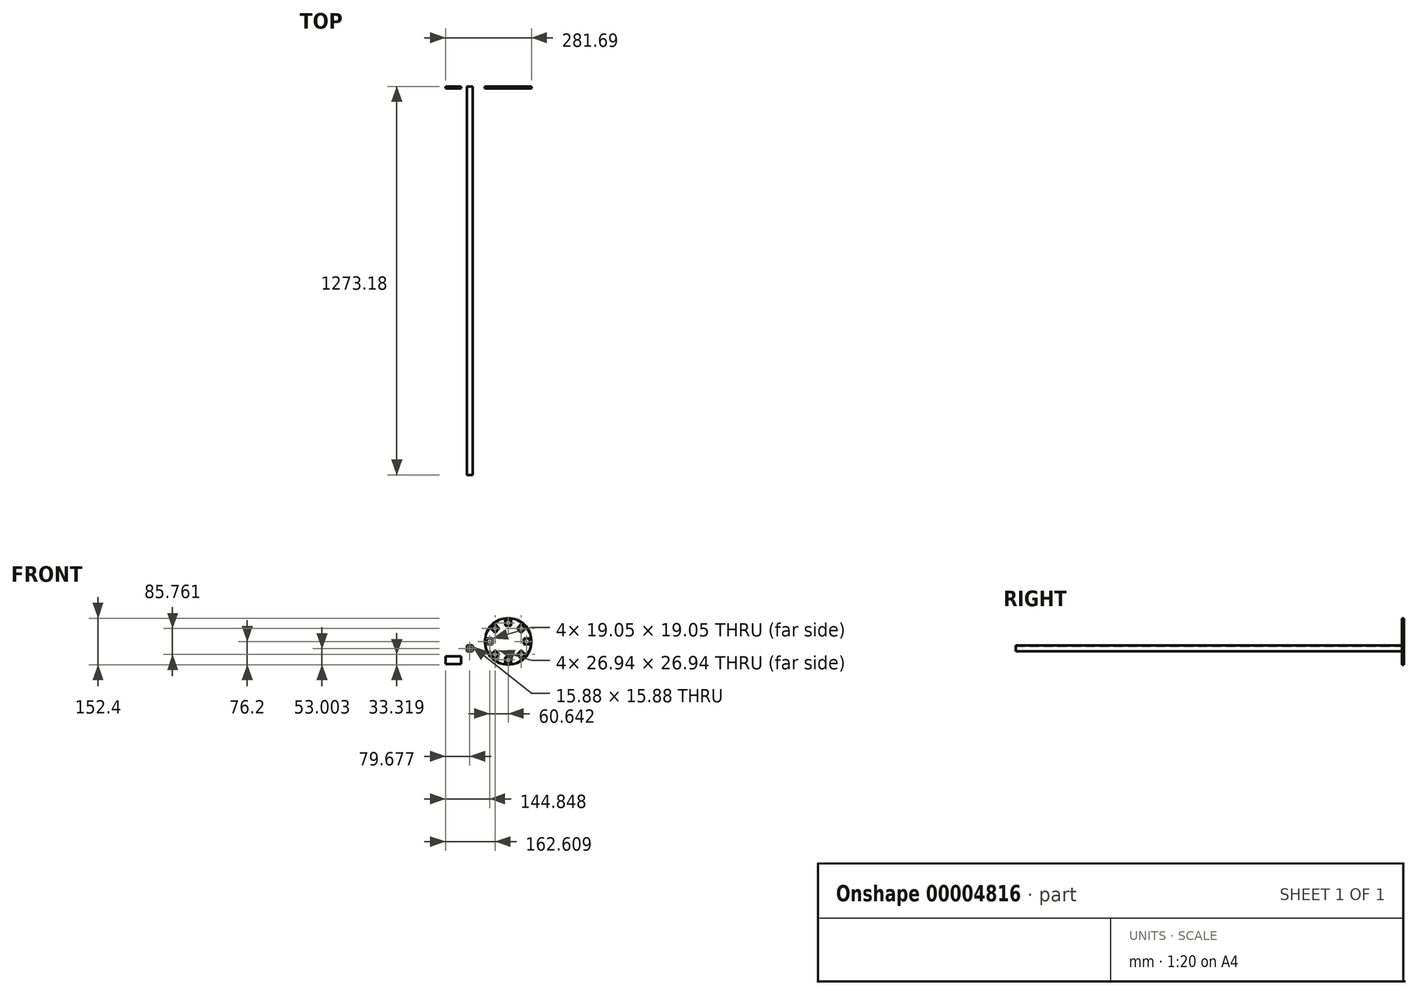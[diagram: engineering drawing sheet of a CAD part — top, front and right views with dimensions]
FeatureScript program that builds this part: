
annotation { "Feature Type Name" : "Feature", "Feature Type Description" : "" }
export const myFeature = defineFeature(function(context is Context, id is Id, definition is map)
    precondition{}
    {
        {
            var Q0;
            Q0=qCreatedBy(makeId("Front.planeOp"),FACE);
            var sketch = newSketch(context, id + "F0", { "sketchPlane" : qUnion([Q0])});
            skCircle(sketch, "E0", {"center": v(0, 0) * mm, "radius": 76.2 * mm});
            skLineSegment(sketch, "E1", {"start": v(0, 60.64) * mm, "end": v(0, 0) * mm, "construction": true});
            skLineSegment(sketch, "E2", {"start": v(123.6, 0) * mm, "end": v(-144.1, 0) * mm, "construction": true});
            skLineSegment(sketch, "E3.rect.bottom", {"start": v(9.53, 51.12) * mm, "end": v(-9.53, 51.12) * mm});
            skLineSegment(sketch, "E3.rect.top", {"start": v(9.53, 70.17) * mm, "end": v(-9.53, 70.17) * mm});
            skLineSegment(sketch, "E3.rect.left", {"start": v(9.52, 51.12) * mm, "end": v(9.53, 70.17) * mm});
            skLineSegment(sketch, "E3.rect.right", {"start": v(-9.53, 51.12) * mm, "end": v(-9.53, 70.17) * mm});
            skPoint(sketch, "E3.rect.middle", {"position": v(0, 60.64) * mm});
            skLineSegment(sketch, "E4.1.0", {"start": v(42.88, 56.35) * mm, "end": v(56.35, 42.88) * mm});
            skLineSegment(sketch, "E4.1.1", {"start": v(29.41, 42.88) * mm, "end": v(42.88, 29.41) * mm});
            skPoint(sketch, "E4.1.2", {"position": v(42.88, 42.88) * mm});
            skLineSegment(sketch, "E4.1.3", {"start": v(42.88, 56.35) * mm, "end": v(29.41, 42.88) * mm});
            skLineSegment(sketch, "E4.1.4", {"start": v(56.35, 42.88) * mm, "end": v(42.88, 29.41) * mm});
            skLineSegment(sketch, "E4.2.0", {"start": v(70.17, 9.53) * mm, "end": v(70.17, -9.53) * mm});
            skLineSegment(sketch, "E4.2.1", {"start": v(51.12, 9.53) * mm, "end": v(51.12, -9.52) * mm});
            skPoint(sketch, "E4.2.2", {"position": v(60.64, 0) * mm});
            skLineSegment(sketch, "E4.2.3", {"start": v(70.17, 9.52) * mm, "end": v(51.12, 9.52) * mm});
            skLineSegment(sketch, "E4.2.4", {"start": v(70.17, -9.53) * mm, "end": v(51.12, -9.53) * mm});
            skLineSegment(sketch, "E5.2.3.0", {"start": v(42.88, -56.35) * mm, "end": v(56.35, -42.88) * mm});
            skLineSegment(sketch, "E5.3.3.0", {"start": v(29.41, -42.88) * mm, "end": v(42.88, -29.41) * mm});
            skPoint(sketch, "E5.6.3.0", {"position": v(42.88, -42.88) * mm});
            skLineSegment(sketch, "E5.7.3.0", {"start": v(42.88, -29.41) * mm, "end": v(56.35, -42.88) * mm});
            skLineSegment(sketch, "E5.10.3.0", {"start": v(29.41, -42.88) * mm, "end": v(42.88, -56.35) * mm});
            skLineSegment(sketch, "E5.2.4.0", {"start": v(-9.52, -70.17) * mm, "end": v(9.53, -70.17) * mm});
            skLineSegment(sketch, "E5.3.4.0", {"start": v(-9.52, -51.12) * mm, "end": v(9.53, -51.12) * mm});
            skPoint(sketch, "E5.6.4.0", {"position": v(0, -60.64) * mm});
            skLineSegment(sketch, "E5.7.4.0", {"start": v(9.52, -51.12) * mm, "end": v(9.52, -70.17) * mm});
            skLineSegment(sketch, "E5.10.4.0", {"start": v(-9.52, -51.12) * mm, "end": v(-9.52, -70.17) * mm});
            skLineSegment(sketch, "E5.2.5.0", {"start": v(-42.88, -56.35) * mm, "end": v(-56.35, -42.88) * mm});
            skLineSegment(sketch, "E5.3.5.0", {"start": v(-29.41, -42.88) * mm, "end": v(-42.88, -29.41) * mm});
            skPoint(sketch, "E5.6.5.0", {"position": v(-42.88, -42.88) * mm});
            skLineSegment(sketch, "E5.7.5.0", {"start": v(-42.88, -56.35) * mm, "end": v(-29.41, -42.88) * mm});
            skLineSegment(sketch, "E5.10.5.0", {"start": v(-56.35, -42.88) * mm, "end": v(-42.88, -29.41) * mm});
            skLineSegment(sketch, "E5.2.6.0", {"start": v(-70.17, -9.53) * mm, "end": v(-70.17, 9.52) * mm});
            skLineSegment(sketch, "E5.3.6.0", {"start": v(-51.12, -9.53) * mm, "end": v(-51.12, 9.52) * mm});
            skPoint(sketch, "E5.6.6.0", {"position": v(-60.64, 0) * mm});
            skLineSegment(sketch, "E5.7.6.0", {"start": v(-70.17, -9.53) * mm, "end": v(-51.12, -9.53) * mm});
            skLineSegment(sketch, "E5.10.6.0", {"start": v(-70.17, 9.52) * mm, "end": v(-51.12, 9.52) * mm});
            skLineSegment(sketch, "E5.2.7.0", {"start": v(-42.88, 56.35) * mm, "end": v(-56.35, 42.88) * mm});
            skLineSegment(sketch, "E5.3.7.0", {"start": v(-29.41, 42.88) * mm, "end": v(-42.88, 29.41) * mm});
            skPoint(sketch, "E5.6.7.0", {"position": v(-42.88, 42.88) * mm});
            skLineSegment(sketch, "E5.7.7.0", {"start": v(-42.88, 29.41) * mm, "end": v(-56.35, 42.88) * mm});
            skLineSegment(sketch, "E5.10.7.0", {"start": v(-29.41, 42.88) * mm, "end": v(-42.88, 56.35) * mm});
            skLineSegment(sketch, "E6.rect.bottom", {"start": v(-116.29, -32.72) * mm, "end": v(-135.34, -32.72) * mm});
            skLineSegment(sketch, "E6.rect.top", {"start": v(-116.29, -13.67) * mm, "end": v(-135.34, -13.67) * mm});
            skLineSegment(sketch, "E6.rect.left", {"start": v(-116.29, -32.72) * mm, "end": v(-116.29, -13.67) * mm});
            skLineSegment(sketch, "E6.rect.right", {"start": v(-135.34, -32.72) * mm, "end": v(-135.34, -13.67) * mm});
            skPoint(sketch, "E6.rect.middle", {"position": v(-125.81, -23.2) * mm});
            skLineSegment(sketch, "E7.rect.bottom", {"start": v(-117.88, -31.13) * mm, "end": v(-133.75, -31.13) * mm});
            skLineSegment(sketch, "E7.rect.top", {"start": v(-117.88, -15.26) * mm, "end": v(-133.75, -15.26) * mm});
            skLineSegment(sketch, "E7.rect.left", {"start": v(-117.88, -31.13) * mm, "end": v(-117.88, -15.26) * mm});
            skLineSegment(sketch, "E7.rect.right", {"start": v(-133.75, -31.13) * mm, "end": v(-133.75, -15.26) * mm});
            skLineSegment(sketch, "E8.rect.bottom", {"start": v(-154.7, -74.03) * mm, "end": v(-205.5, -74.03) * mm});
            skLineSegment(sketch, "E8.rect.top", {"start": v(-154.7, -48.63) * mm, "end": v(-205.5, -48.63) * mm});
            skLineSegment(sketch, "E8.rect.left", {"start": v(-154.7, -74.03) * mm, "end": v(-154.7, -48.63) * mm});
            skLineSegment(sketch, "E8.rect.right", {"start": v(-205.5, -74.03) * mm, "end": v(-205.5, -48.63) * mm});
            skPoint(sketch, "E8.rect.middle", {"position": v(-180.1, -61.33) * mm});
            skLineSegment(sketch, "E9.rect.bottom", {"start": v(-95.87, -111.37) * mm, "end": v(-114.92, -111.37) * mm, "construction": true});
            skLineSegment(sketch, "E9.rect.top", {"start": v(-95.87, -92.32) * mm, "end": v(-114.92, -92.32) * mm, "construction": true});
            skLineSegment(sketch, "E9.rect.left", {"start": v(-95.87, -111.37) * mm, "end": v(-95.87, -92.32) * mm, "construction": true});
            skLineSegment(sketch, "E9.rect.right", {"start": v(-114.92, -111.37) * mm, "end": v(-114.92, -92.32) * mm, "construction": true});
            skPoint(sketch, "E9.rect.middle", {"position": v(-105.4, -101.84) * mm});
            skLineSegment(sketch, "E10.rect.bottom", {"start": v(-215.94, -117.06) * mm, "end": v(-234.99, -117.06) * mm, "construction": true});
            skLineSegment(sketch, "E10.rect.top", {"start": v(-215.94, -98.01) * mm, "end": v(-234.99, -98.01) * mm, "construction": true});
            skPoint(sketch, "E10.rect.middle", {"position": v(-225.46, -107.54) * mm});
            skLineSegment(sketch, "E10.rect.left", {"start": v(-215.94, -117.06) * mm, "end": v(-215.94, -98.01) * mm, "construction": true});
            skLineSegment(sketch, "E10.rect.right", {"start": v(-234.99, -117.06) * mm, "end": v(-234.99, -98.01) * mm, "construction": true});
            skSolve(sketch);
        }
        {
            var Q0;
            Q0 = qSketchRegion(id + "F0", true);
            extrude(context, id + "F1", {"entities" : qUnion([Q0]), "endBound" : BoundingType.SYMMETRIC, "depth" : 6.35 * mm});
        }
        {
            var Q0;
            Q0=makeQuery(id+"F0.imprint","IMPRINT",FACE,{"disambiguationData":[TD([[makeQuery(id+"F0.imprint","IMPRINT",EDGE,{"derivedFrom":sQuery(id+"F0.wireOp",EDGE,"E6.rect.bottom")}),-1.0]])]});
            extrude(context, id + "F2", {"entities" : qUnion([Q0]), "operationType" : NewBodyOperationType.ADD, "depth" : 1270 * mm});
        }
    });
